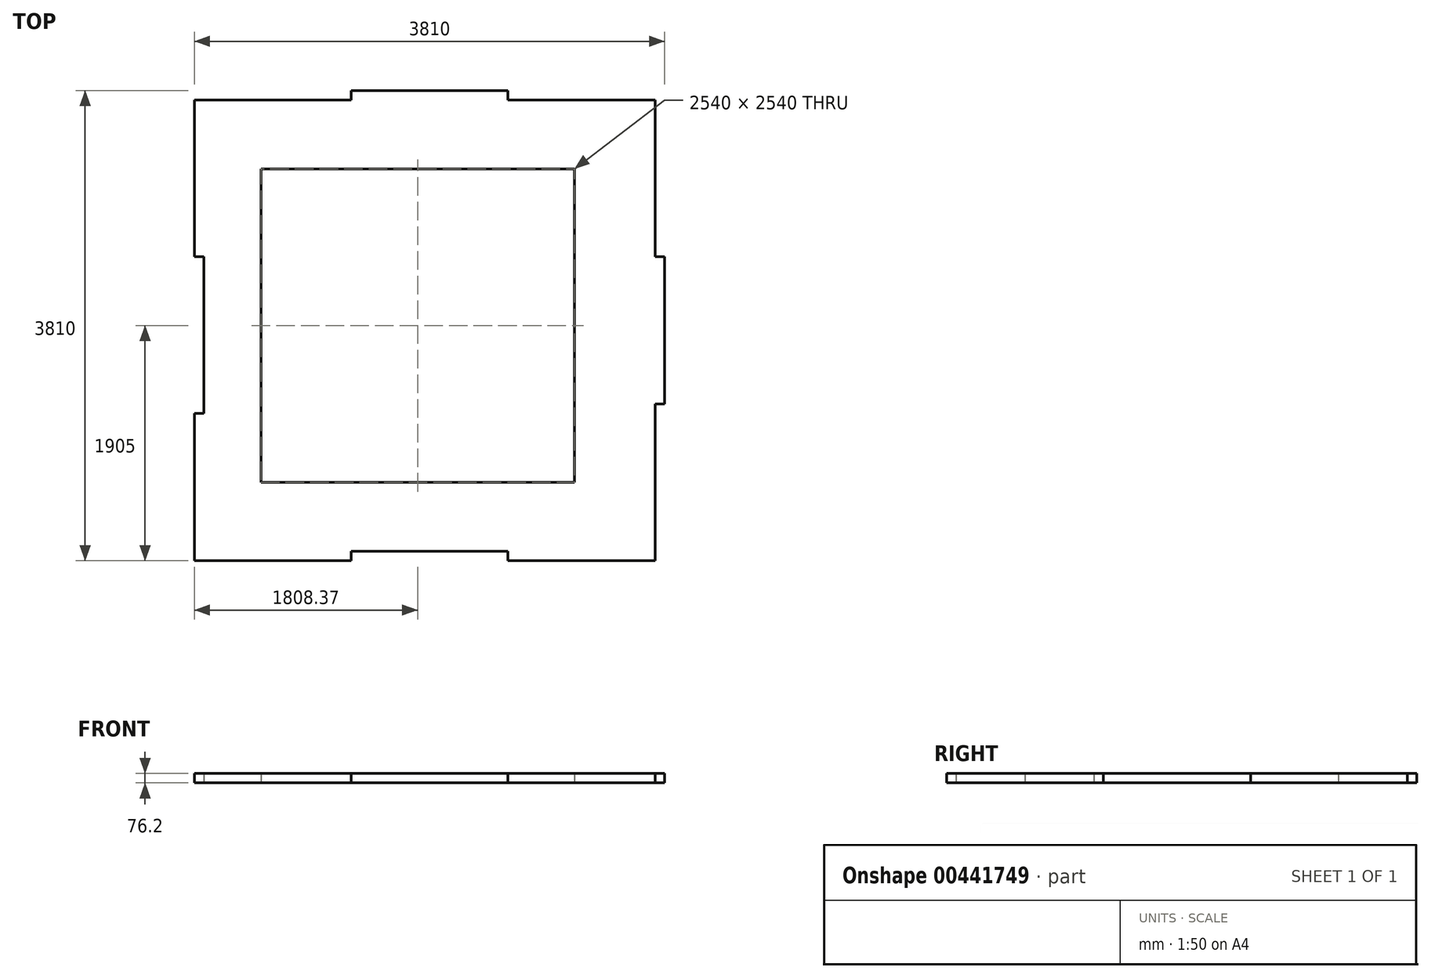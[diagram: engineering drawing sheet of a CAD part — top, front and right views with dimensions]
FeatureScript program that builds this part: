
annotation { "Feature Type Name" : "Feature", "Feature Type Description" : "" }
export const myFeature = defineFeature(function(context is Context, id is Id, definition is map)
    precondition{}
    {
        {
            var Q0;
            Q0=qCreatedBy(makeId("Top.planeOp"),FACE);
            var sketch = newSketch(context, id + "F0", { "sketchPlane" : qUnion([Q0])});
            skLineSegment(sketch, "E0.bottom", {"start": v(731.63, 1905) * mm, "end": v(-538.37, 1905) * mm});
            skLineSegment(sketch, "E0.top", {"start": v(1925.43, -1905) * mm, "end": v(731.63, -1905) * mm});
            skLineSegment(sketch, "E0.left", {"start": v(2001.63, 558.8) * mm, "end": v(2001.63, -635) * mm});
            skLineSegment(sketch, "E0.right", {"start": v(-1808.37, 1828.8) * mm, "end": v(-1808.37, 558.8) * mm});
            skPoint(sketch, "E0.middle", {"position": v(96.63, 0) * mm});
            skLineSegment(sketch, "E1", {"start": v(-1808.37, 1828.8) * mm, "end": v(-538.37, 1828.8) * mm});
            skLineSegment(sketch, "E2", {"start": v(-538.37, 1828.8) * mm, "end": v(-538.37, 1905) * mm});
            skLineSegment(sketch, "E3", {"start": v(1925.43, 1828.8) * mm, "end": v(731.63, 1828.8) * mm});
            skLineSegment(sketch, "E4", {"start": v(731.63, 1828.8) * mm, "end": v(731.63, 1905) * mm});
            skLineSegment(sketch, "E5", {"start": v(-1808.37, -1905) * mm, "end": v(-538.37, -1905) * mm});
            skLineSegment(sketch, "E6", {"start": v(-538.37, -1905) * mm, "end": v(-538.37, -1828.8) * mm});
            skLineSegment(sketch, "E7", {"start": v(-538.37, -1828.8) * mm, "end": v(731.63, -1828.8) * mm});
            skLineSegment(sketch, "E8", {"start": v(731.63, -1828.8) * mm, "end": v(731.63, -1905) * mm});
            skLineSegment(sketch, "E9.trimOffspring", {"start": v(-538.37, -1905) * mm, "end": v(-1808.37, -1905) * mm});
            skPoint(sketch, "E10.orphan", {"position": v(-1808.37, 1905) * mm});
            skPoint(sketch, "E11.orphan", {"position": v(2001.63, 1905) * mm});
            skLineSegment(sketch, "E12", {"start": v(-1808.37, 558.8) * mm, "end": v(-1732.17, 558.8) * mm});
            skLineSegment(sketch, "E13", {"start": v(-1732.17, 558.8) * mm, "end": v(-1732.17, -711.2) * mm});
            skLineSegment(sketch, "E14", {"start": v(-1732.17, -711.2) * mm, "end": v(-1808.37, -711.2) * mm});
            skLineSegment(sketch, "E15.trimOffspring", {"start": v(-1808.37, -711.2) * mm, "end": v(-1808.37, -1905) * mm});
            skLineSegment(sketch, "E16", {"start": v(1925.43, -1905) * mm, "end": v(1925.43, -635) * mm});
            skLineSegment(sketch, "E17", {"start": v(1925.43, -635) * mm, "end": v(2001.63, -635) * mm});
            skPoint(sketch, "E18.orphan", {"position": v(2001.63, -1905) * mm});
            skLineSegment(sketch, "E19", {"start": v(1925.43, 558.8) * mm, "end": v(2001.63, 558.8) * mm});
            skLineSegment(sketch, "E20", {"start": v(1925.43, 558.8) * mm, "end": v(1925.43, 1828.8) * mm});
            skLineSegment(sketch, "E21.bottom", {"start": v(1270, 1270) * mm, "end": v(-1270, 1270) * mm});
            skLineSegment(sketch, "E21.top", {"start": v(1270, -1270) * mm, "end": v(-1270, -1270) * mm});
            skLineSegment(sketch, "E21.left", {"start": v(1270, 1270) * mm, "end": v(1270, -1270) * mm});
            skLineSegment(sketch, "E21.right", {"start": v(-1270, 1270) * mm, "end": v(-1270, -1270) * mm});
            skPoint(sketch, "E21.middle", {"position": v(0, 0) * mm});
            skSolve(sketch);
        }
        {
            var Q0;
            Q0=makeQuery(id+"F0.imprint","IMPRINT",FACE,{"disambiguationData":[TD([[makeQuery(id+"F0.imprint","IMPRINT",EDGE,{"derivedFrom":sQuery(id+"F0.wireOp",EDGE,"E0.bottom")}),1.0]])]});
            extrude(context, id + "F1", {"entities" : qUnion([Q0]), "depth" : 76.2 * mm});
        }
    });
